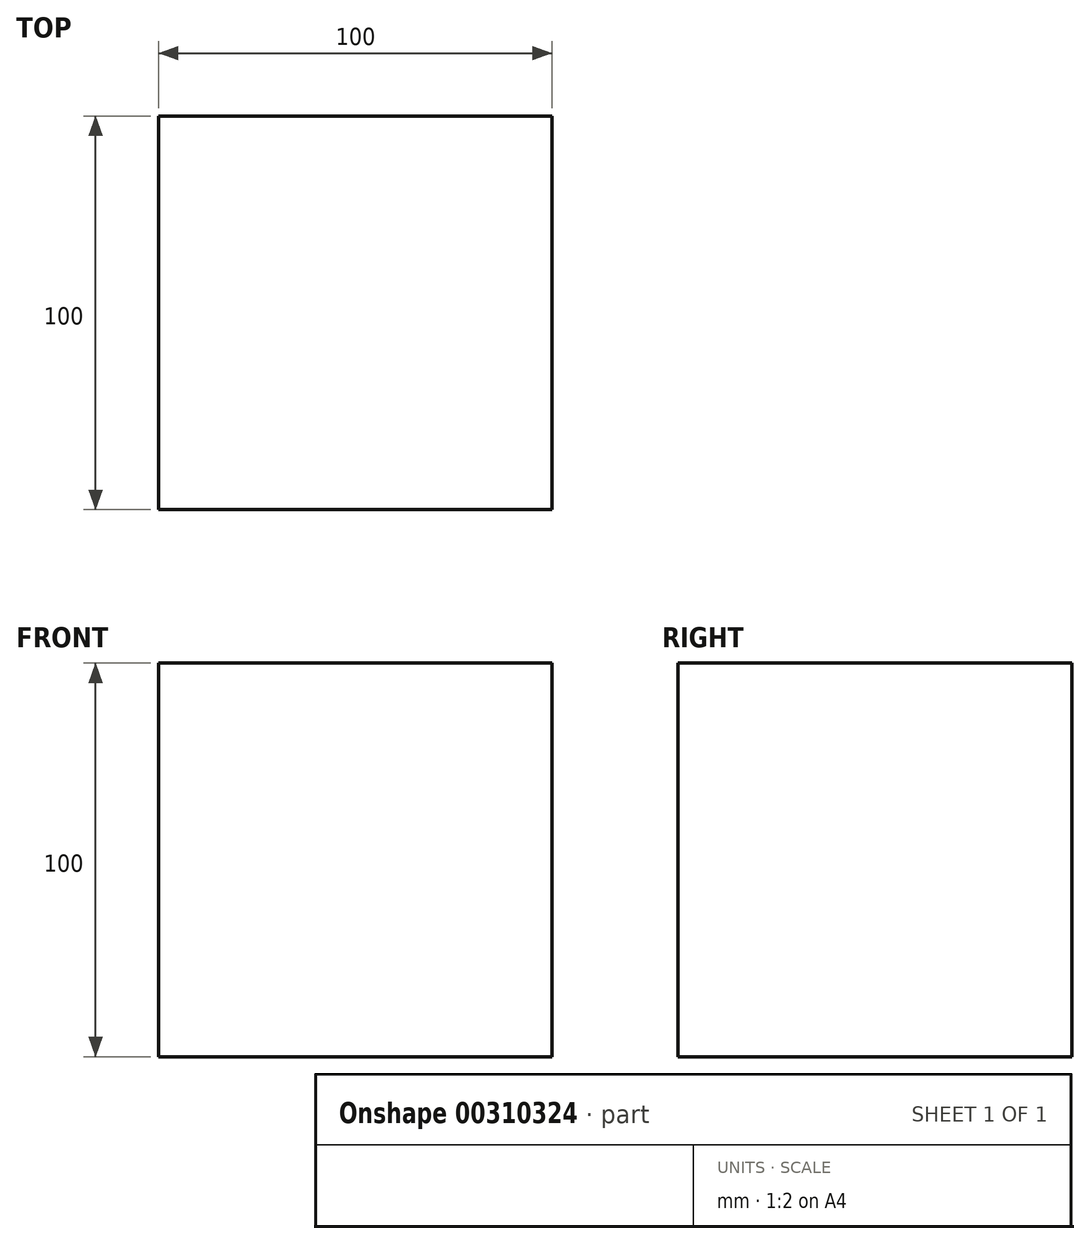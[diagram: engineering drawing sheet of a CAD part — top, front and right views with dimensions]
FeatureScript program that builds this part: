
annotation { "Feature Type Name" : "Feature", "Feature Type Description" : "" }
export const myFeature = defineFeature(function(context is Context, id is Id, definition is map)
    precondition{}
    {
        {
            var Q0;
            Q0=qCreatedBy(makeId("Top.planeOp"),FACE);
            var sketch = newSketch(context, id + "F0", { "sketchPlane" : qUnion([Q0])});
            skLineSegment(sketch, "E0.bottom", {"start": v(100, 100) * mm, "end": v(0, 100) * mm});
            skLineSegment(sketch, "E0.top", {"start": v(100, 0) * mm, "end": v(0, 0) * mm});
            skLineSegment(sketch, "E0.left", {"start": v(100, 100) * mm, "end": v(100, 0) * mm});
            skLineSegment(sketch, "E0.right", {"start": v(0, 100) * mm, "end": v(0, 0) * mm});
            skSolve(sketch);
        }
        {
            var Q0;
            Q0=makeQuery(id+"F0.imprint","IMPRINT",FACE,{"disambiguationData":[TD([[makeQuery(id+"F0.imprint","IMPRINT",EDGE,{"derivedFrom":sQuery(id+"F0.wireOp",EDGE,"E0.bottom")}),1.0]])]});
            extrude(context, id + "F1", {"entities" : qUnion([Q0]), "depth" : 100 * mm});
        }
    });
